# Revit family: Accessory-Towel_Bar-KOHLER-OCCASION-K-27085_1
name_source: partatom
category: Specialty Equipment
revit_build: Autodesk Revit 2017 (Build: 20160225_1515(x64)
units: mm (PartAtom-declared; Revit-internal decimal feet)

## family parameters
Cut with Voids When Loaded = No
Host = Face
OmniClass Number = 23.31.25.25
OmniClass Title = Towel Bars
Part Type = Normal
Room Calculation Point = No
Round Connector Dimension = Use Diameter
Shared = No

## types (6) — shared parameters
ADA Compliant = No
Assembly Code = C1030200
Date Modified = 11/11/2021
Default Elevation = 42"
Description = CLASSICAL, DOUBLE TOWEL SHELF
Height = 6 7/8"
Length = 11 13/16"
Manufacturer = KOHLER Co.
Master Format 2014 = 10 28 00
Master Format 2014 Name = Toilet, Bath, and Laundry Accessories
Material = Premium Metal Construction
Product Documentation Link = https://www.us.kohler.com
Product Name = OCCASION
Product Page URL = http://www.us.kohler.com
URL = https://www.us.kohler.com
WaterSense Certified = No
Width = 24"

## per-type parameters (varying)
| type | Finish | Model | Secondary Finish | Type |
| 2MB-Vibrant Brushed Moderne Brass | Kohler-Metal-2MB-Vibrant_Brushed_Moderne_Brass | K-27085-2MB | Kohler-Metal-2MB-Vibrant_Brushed_Moderne_Brass | 1 |
| BL-Matte Black | Kohler-Metal-BL-Matte_Black | K-27085-BL | Kohler-Metal-BL-Matte_Black | 2 |
| BMB-Matte Black With Moderne Brass | Kohler-Metal-BL-Matte_Black | K-27085-BMB | Kohler-Metal-2MB-Vibrant_Brushed_Moderne_Brass | 3 |
| BN-Vibrant Brushed Nickel | Kohler-Metal-BN-Vibrant_Brushed_Nickel | K-27085-BN | Kohler-Metal-BN-Vibrant_Brushed_Nickel | 4 |
| CP-Polished Chrome | Kohler-Metal-CP-Polished_Chrome | K-27085-CP | Kohler-Metal-CP-Polished_Chrome | 5 |
| SN-Vibrant Polished Nickel | Kohler-Metal-SN-Vibrant_Polished_Nickel | K-27085-SN | Kohler-Metal-SN-Vibrant_Polished_Nickel | 6 |

## geometry (parser evidence)
native form markers: Sweep x5
no freeform markers — native parametric forms only
